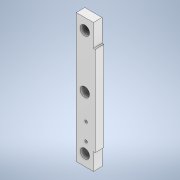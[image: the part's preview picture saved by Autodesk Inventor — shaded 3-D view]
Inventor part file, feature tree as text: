
AUTODESK INVENTOR PART (.ipt)
format: ipt  version: 2020 (Build 240168000, 168)  size: 149,504 bytes
history: native  units: mm
features: other x1, sketch x1, extrude x1
ambient origin geometry x8: Origin, YZ Plane, XZ Plane, XY Plane, X Axis, Y Axis, Z Axis, Center Point
bodies: Body1 (feature_tree)
feature tree (3):
  other  "Bryła1"
  sketch  "Szkic1"
  extrude  "Wyciągnięcie proste1"  Depth=75.0mm
